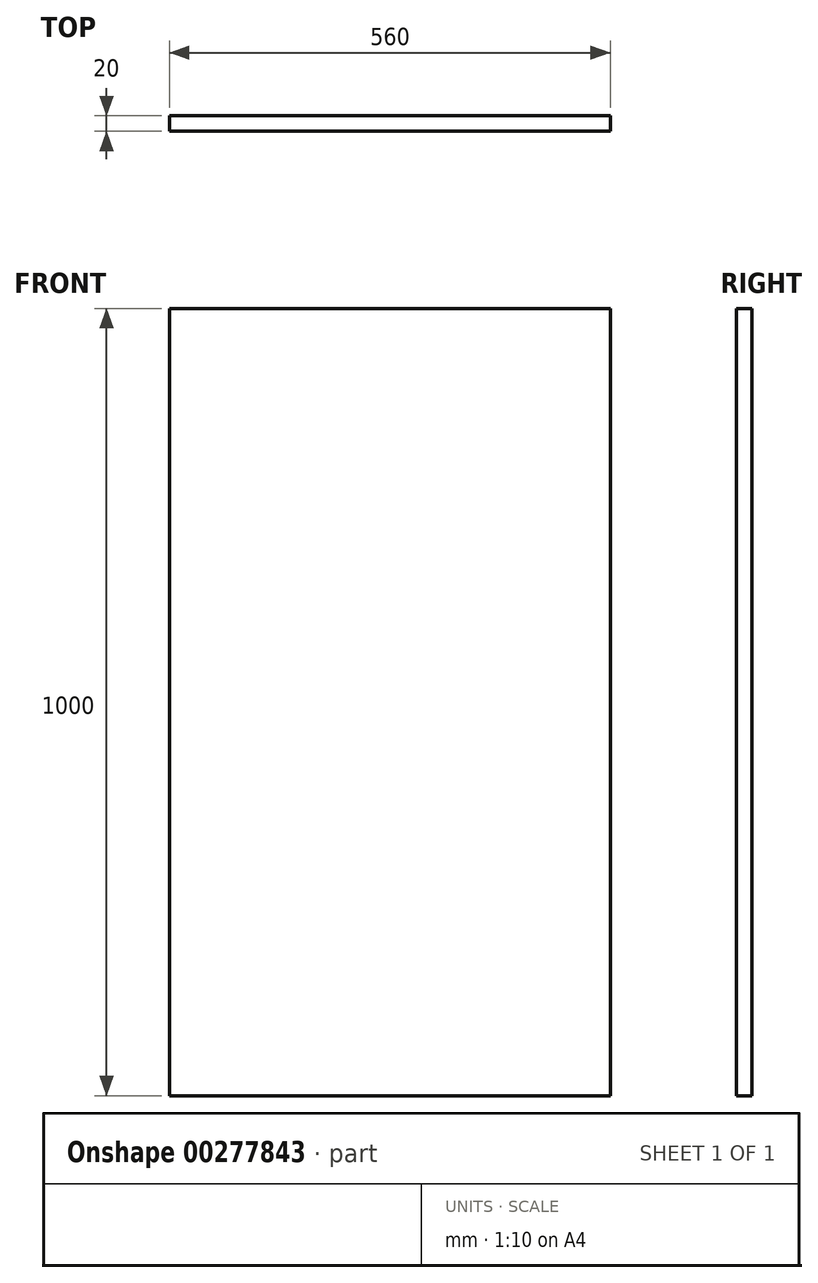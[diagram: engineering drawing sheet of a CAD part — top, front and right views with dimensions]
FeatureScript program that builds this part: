
annotation { "Feature Type Name" : "Feature", "Feature Type Description" : "" }
export const myFeature = defineFeature(function(context is Context, id is Id, definition is map)
    precondition{}
    {
        {
            var Q0;
            Q0=qCreatedBy(makeId("Front.planeOp"),FACE);
            var sketch = newSketch(context, id + "F0", { "sketchPlane" : qUnion([Q0])});
            skLineSegment(sketch, "E0.bottom", {"start": v(-560, -1000) * mm, "end": v(0, -1000) * mm});
            skLineSegment(sketch, "E0.top", {"start": v(-560, 0) * mm, "end": v(0, 0) * mm});
            skLineSegment(sketch, "E0.left", {"start": v(-560, -1000) * mm, "end": v(-560, 0) * mm});
            skLineSegment(sketch, "E0.right", {"start": v(0, -1000) * mm, "end": v(0, 0) * mm});
            skSolve(sketch);
        }
        {
            var Q0;
            Q0=qSketchRegion(id+"F0",true);
            extrude(context, id + "F1", {"entities" : qUnion([Q0]), "depth" : 20 * mm});
        }
    });
